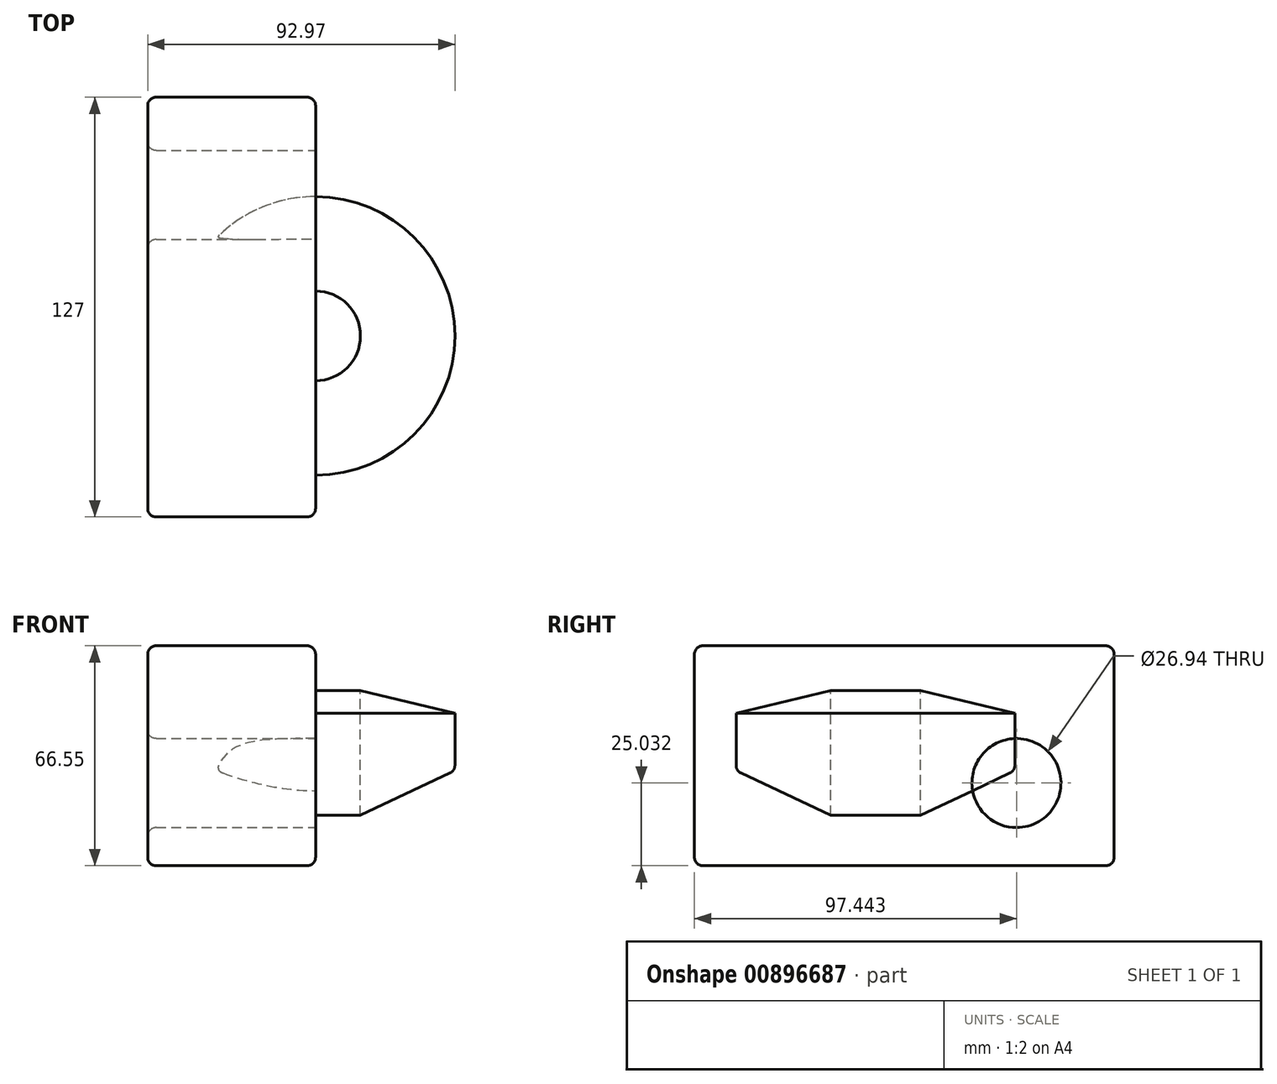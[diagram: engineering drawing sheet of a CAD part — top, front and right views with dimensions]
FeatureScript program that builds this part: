
annotation { "Feature Type Name" : "Feature", "Feature Type Description" : "" }
export const myFeature = defineFeature(function(context is Context, id is Id, definition is map)
    precondition{}
    {
        {
            var Q0;
            Q0=qCreatedBy(makeId("Top.planeOp"),FACE);
            var sketch = newSketch(context, id + "F0", { "sketchPlane" : qUnion([Q0])});
            skLineSegment(sketch, "E0.bottom", {"start": v(0, 63.72) * mm, "end": v(50.8, 63.72) * mm});
            skLineSegment(sketch, "E0.top", {"start": v(0, -63.28) * mm, "end": v(50.8, -63.28) * mm});
            skLineSegment(sketch, "E0.left", {"start": v(0, 63.72) * mm, "end": v(0, -63.28) * mm});
            skLineSegment(sketch, "E0.right", {"start": v(50.8, 63.72) * mm, "end": v(50.8, -63.28) * mm});
            skSolve(sketch);
        }
        {
            var Q0;
            Q0 = qSketchRegion(id + "F0", true);
            extrude(context, id + "F1", {"entities" : qUnion([Q0]), "depth" : 66.55 * mm, "offsetDistance" : 25.4 * mm});
        }
        {
            var Q0;
            Q0=makeQuery(id+"F1.opExtrude","SWEPT_FACE",FACE,{"disambiguationData":[OSD([sQuery(id+"F0.wireOp",EDGE,"E0.right")])]});
            var sketch = newSketch(context, id + "F2", { "sketchPlane" : qUnion([Q0])});
            skCircle(sketch, "E1", {"center": v(34.16, 25.03) * mm, "radius": 13.47 * mm});
            skSolve(sketch);
        }
        {
            var Q0;
            Q0 = qSketchRegion(id + "F2", true);
            extrude(context, id + "F3", {"entities" : qUnion([Q0]), "operationType" : NewBodyOperationType.REMOVE, "oppositeDirection" : true, "depth" : 86.61 * mm, "offsetDistance" : 25.4 * mm});
        }
        {
            var Q0;
            Q0=makeQuery(id+"F1.opExtrude","SWEPT_FACE",FACE,{"disambiguationData":[OSD([sQuery(id+"F0.wireOp",EDGE,"E0.right")])]});
            var sketch = newSketch(context, id + "F4", { "sketchPlane" : qUnion([Q0])});
            skLineSegment(sketch, "E2", {"start": v(-22.08, 15.25) * mm, "end": v(-22.08, 52.97) * mm});
            skLineSegment(sketch, "E3", {"start": v(-22.08, 52.97) * mm, "end": v(-50.67, 46.19) * mm});
            skLineSegment(sketch, "E4", {"start": v(-50.67, 46.19) * mm, "end": v(-50.67, 28.75) * mm});
            skLineSegment(sketch, "E5", {"start": v(-50.67, 28.75) * mm, "end": v(-22.08, 15.25) * mm});
            skLineSegment(sketch, "E6", {"start": v(-8.5, 58.11) * mm, "end": v(-8.5, 15.25) * mm});
            skSolve(sketch);
        }
        {
            var Q0;
            Q0=makeQuery(id+"F4.imprint","IMPRINT",FACE,{"disambiguationData":[TD([[makeQuery(id+"F4.imprint","IMPRINT",EDGE,{"derivedFrom":sQuery(id+"F4.wireOp",EDGE,"E2")}),1.0]])]});
            var Q1;
            Q1=sQuery(id+"F4.wireOp",EDGE,"E6");
            revolve(context, id + "F5", {"operationType" : NewBodyOperationType.ADD, "surfaceOperationType" : NewSurfaceOperationType.NEW, "entities" : qUnion([Q0]), "axis" : qUnion([Q1]), "revolveType" : RevolveType.FULL});
        }
        {
            var Q0;
            Q0=makeQuery(id+"F1.opExtrude","CAP_EDGE",EDGE,{"disambiguationData":[OSD([sQuery(id+"F0.wireOp",EDGE,"E0.left")])],"isStart":true});
            var Q1;
            Q1=makeQuery(id+"F1.opExtrude","CAP_EDGE",EDGE,{"disambiguationData":[OSD([sQuery(id+"F0.wireOp",EDGE,"E0.bottom")])],"isStart":true});
            var Q2;
            Q2=makeQuery(id+"F1.opExtrude","CAP_EDGE",EDGE,{"disambiguationData":[OSD([sQuery(id+"F0.wireOp",EDGE,"E0.right")])],"isStart":true});
            var Q3;
            Q3=makeQuery(id+"F1.opExtrude","CAP_EDGE",EDGE,{"disambiguationData":[OSD([sQuery(id+"F0.wireOp",EDGE,"E0.top")])],"isStart":true});
            var Q4;
            Q4=makeQuery(id+"F1.opExtrude","SWEPT_EDGE",EDGE,{"disambiguationData":[OSD([sQuery(id+"F0.wireOp",EDGE,"E0.bottom"),sQuery(id+"F0.wireOp",EDGE,"E0.right")])]});
            var Q5;
            Q5=makeQuery(id+"F1.opExtrude","CAP_EDGE",EDGE,{"disambiguationData":[OSD([sQuery(id+"F0.wireOp",EDGE,"E0.right")])],"isStart":false});
            var Q6;
            Q6=makeQuery(id+"F1.opExtrude","SWEPT_EDGE",EDGE,{"disambiguationData":[OSD([sQuery(id+"F0.wireOp",EDGE,"E0.top"),sQuery(id+"F0.wireOp",EDGE,"E0.right")])]});
            var Q7;
            Q7=makeQuery(id+"F1.opExtrude","CAP_EDGE",EDGE,{"disambiguationData":[OSD([sQuery(id+"F0.wireOp",EDGE,"E0.top")])],"isStart":false});
            var Q8;
            Q8=makeQuery(id+"F1.opExtrude","SWEPT_EDGE",EDGE,{"disambiguationData":[OSD([sQuery(id+"F0.wireOp",EDGE,"E0.top"),sQuery(id+"F0.wireOp",EDGE,"E0.left")])]});
            var Q9;
            Q9=makeQuery(id+"F1.opExtrude","SWEPT_FACE",FACE,{"disambiguationData":[OSD([sQuery(id+"F0.wireOp",EDGE,"E0.left")])]});
            var Q10;
            Q10=makeQuery(id+"F1.opExtrude","CAP_FACE",FACE,{"disambiguationData":[OSD([sQuery(id+"F0.wireOp",EDGE,"E0.bottom"),sQuery(id+"F0.wireOp",EDGE,"E0.top"),sQuery(id+"F0.wireOp",EDGE,"E0.left"),sQuery(id+"F0.wireOp",EDGE,"E0.right")])],"isStart":false});
            var Q11;
            Q11=makeQuery(id+"F1.opExtrude","SWEPT_FACE",FACE,{"disambiguationData":[OSD([sQuery(id+"F0.wireOp",EDGE,"E0.bottom")])]});
            fillet(context, id + "F6", {"entities" : qUnion([Q0, Q1, Q2, Q3, Q4, Q5, Q6, Q7, Q8, Q9, Q10, Q11]), "radius" : 2.54 * mm, "tangentPropagation" : true, "allowEdgeOverflow" : false});
        }
        {
            var Q0;
            Q0=makeQuery(id+"F5.opRevolve","SWEPT_EDGE",EDGE,{"disambiguationData":[OSD([sQuery(id+"F4.wireOp",EDGE,"E4"),sQuery(id+"F4.wireOp",EDGE,"E5")])]});
            fillet(context, id + "F7", {"entities" : qUnion([Q0]), "radius" : 2.54 * mm, "tangentPropagation" : true, "allowEdgeOverflow" : false});
        }
    });
